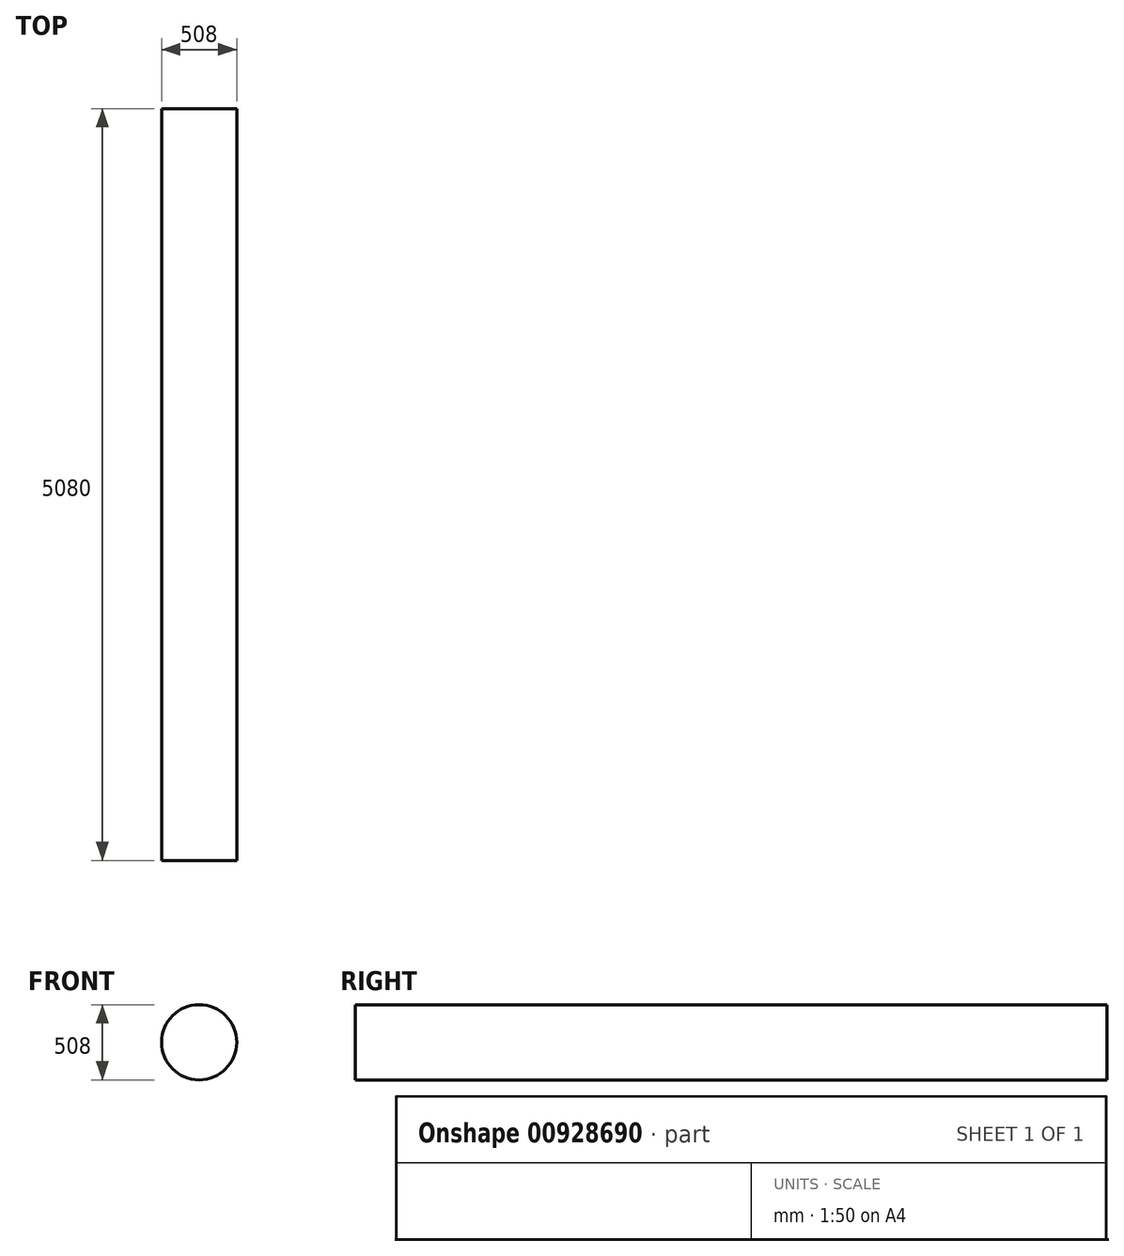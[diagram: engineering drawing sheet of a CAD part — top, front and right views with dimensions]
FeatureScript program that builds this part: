
annotation { "Feature Type Name" : "Feature", "Feature Type Description" : "" }
export const myFeature = defineFeature(function(context is Context, id is Id, definition is map)
    precondition{}
    {
        {
            var Q0;
            Q0=qCreatedBy(makeId("Front.planeOp"),FACE);
            var sketch = newSketch(context, id + "F0", { "sketchPlane" : qUnion([Q0])});
            skCircle(sketch, "E0", {"center": v(0, 0) * mm, "radius": 254 * mm});
            skSolve(sketch);
        }
        {
            var Q0;
            Q0 = qSketchRegion(id + "F0", true);
            extrude(context, id + "F1", {"entities" : qUnion([Q0]), "depth" : 5080 * mm, "offsetDistance" : 25.4 * mm});
        }
    });
